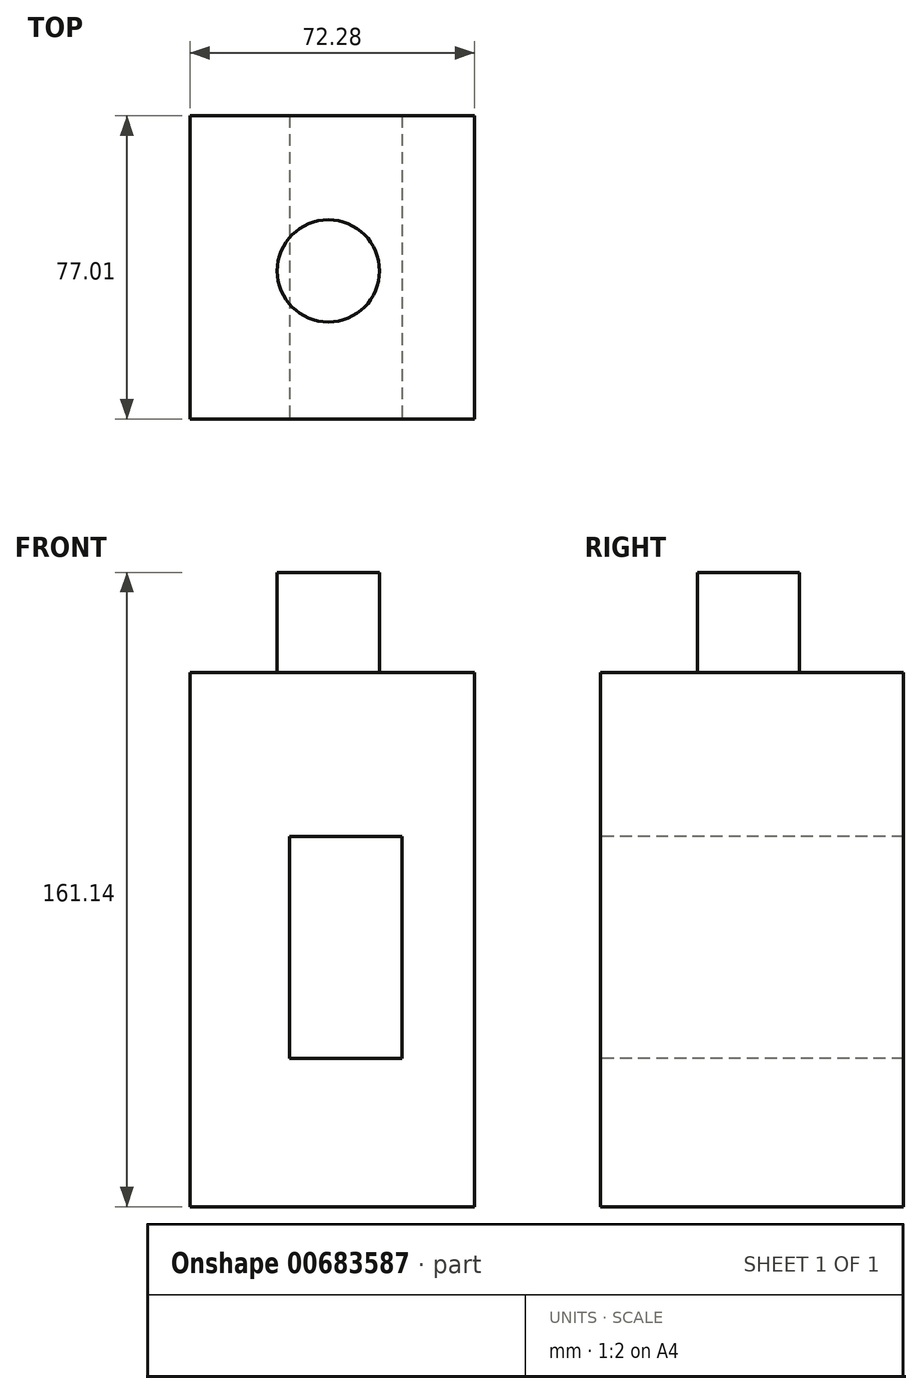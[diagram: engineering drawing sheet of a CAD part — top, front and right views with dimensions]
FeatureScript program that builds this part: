
annotation { "Feature Type Name" : "Feature", "Feature Type Description" : "" }
export const myFeature = defineFeature(function(context is Context, id is Id, definition is map)
    precondition{}
    {
        {
            var Q0;
            Q0=qCreatedBy(makeId("Right.planeOp"),FACE);
            var sketch = newSketch(context, id + "F0", { "sketchPlane" : qUnion([Q0])});
            skLineSegment(sketch, "E0.bottom", {"start": v(-63.32, 128.9) * mm, "end": v(13.69, 128.9) * mm});
            skLineSegment(sketch, "E0.top", {"start": v(-63.32, -6.84) * mm, "end": v(13.69, -6.84) * mm});
            skLineSegment(sketch, "E0.left", {"start": v(-63.32, 128.9) * mm, "end": v(-63.32, -6.84) * mm});
            skLineSegment(sketch, "E0.right", {"start": v(13.69, 128.9) * mm, "end": v(13.69, -6.84) * mm});
            skSolve(sketch);
        }
        {
            var Q0;
            Q0 = qSketchRegion(id + "F0", true);
            extrude(context, id + "F1", {"entities" : qUnion([Q0]), "depth" : 72.28 * mm, "offsetDistance" : 25.4 * mm});
        }
        {
            var Q0;
            Q0=makeQuery(id+"F1.opExtrude","SWEPT_FACE",FACE,{"disambiguationData":[OSD([sQuery(id+"F0.wireOp",EDGE,"E0.bottom")])]});
            var sketch = newSketch(context, id + "F2", { "sketchPlane" : qUnion([Q0])});
            skCircle(sketch, "E1", {"center": v(35.16, -25.7) * mm, "radius": 12.99 * mm});
            skSolve(sketch);
        }
        {
            var Q0;
            Q0 = qSketchRegion(id + "F2", true);
            extrude(context, id + "F3", {"entities" : qUnion([Q0]), "operationType" : NewBodyOperationType.ADD, "depth" : 25.4 * mm, "offsetDistance" : 25.4 * mm});
        }
        {
            var Q0;
            Q0=makeQuery(id+"F1.opExtrude","CAP_FACE",FACE,{"disambiguationData":[OSD([sQuery(id+"F0.wireOp",EDGE,"E0.bottom"),sQuery(id+"F0.wireOp",EDGE,"E0.top"),sQuery(id+"F0.wireOp",EDGE,"E0.left"),sQuery(id+"F0.wireOp",EDGE,"E0.right")])],"isStart":false});
            var sketch = newSketch(context, id + "F4", { "sketchPlane" : qUnion([Q0])});
            skLineSegment(sketch, "E2.bottom", {"start": v(-37.38, 75.28) * mm, "end": v(-14.77, 75.28) * mm});
            skLineSegment(sketch, "E2.top", {"start": v(-37.38, 38.43) * mm, "end": v(-14.77, 38.43) * mm});
            skLineSegment(sketch, "E2.left", {"start": v(-37.38, 75.28) * mm, "end": v(-37.38, 38.43) * mm});
            skLineSegment(sketch, "E2.right", {"start": v(-14.77, 75.28) * mm, "end": v(-14.77, 38.43) * mm});
            skSolve(sketch);
        }
        {
            var Q0;
            Q0=makeQuery(id+"F4.imprint","IMPRINT",FACE,{"disambiguationData":[TD([[makeQuery(id+"F4.imprint","IMPRINT",EDGE,{"derivedFrom":sQuery(id+"F4.wireOp",EDGE,"E2.bottom")}),-1.0]])]});
            var Q1;
            Q1=sQuery(id+"F4.wireOp",EDGE,"E2.right");
            extrude(context, id + "F5", {"entities" : qUnion([Q0]), "operationType" : NewBodyOperationType.REMOVE, "surfaceEntities" : qUnion([Q1]), "depth" : 49.9 * mm, "offsetDistance" : 25.4 * mm});
        }
        {
            var Q0;
            Q0=makeQuery(id+"F1.opExtrude","SWEPT_FACE",FACE,{"disambiguationData":[OSD([sQuery(id+"F0.wireOp",EDGE,"E0.left")])]});
            var sketch = newSketch(context, id + "F6", { "sketchPlane" : qUnion([Q0])});
            skLineSegment(sketch, "E3.bottom", {"start": v(25.36, 87.26) * mm, "end": v(53.93, 87.26) * mm});
            skLineSegment(sketch, "E3.top", {"start": v(25.36, 30.8) * mm, "end": v(53.93, 30.8) * mm});
            skLineSegment(sketch, "E3.left", {"start": v(25.36, 87.26) * mm, "end": v(25.36, 30.8) * mm});
            skLineSegment(sketch, "E3.right", {"start": v(53.93, 87.26) * mm, "end": v(53.93, 30.8) * mm});
            skSolve(sketch);
        }
        {
            var Q0;
            Q0 = qSketchRegion(id + "F6", true);
            extrude(context, id + "F7", {"entities" : qUnion([Q0]), "operationType" : NewBodyOperationType.REMOVE, "endBound" : BoundingType.UP_TO_NEXT, "oppositeDirection" : true, "depth" : 25.4 * mm, "offsetDistance" : 25.4 * mm});
        }
    });
